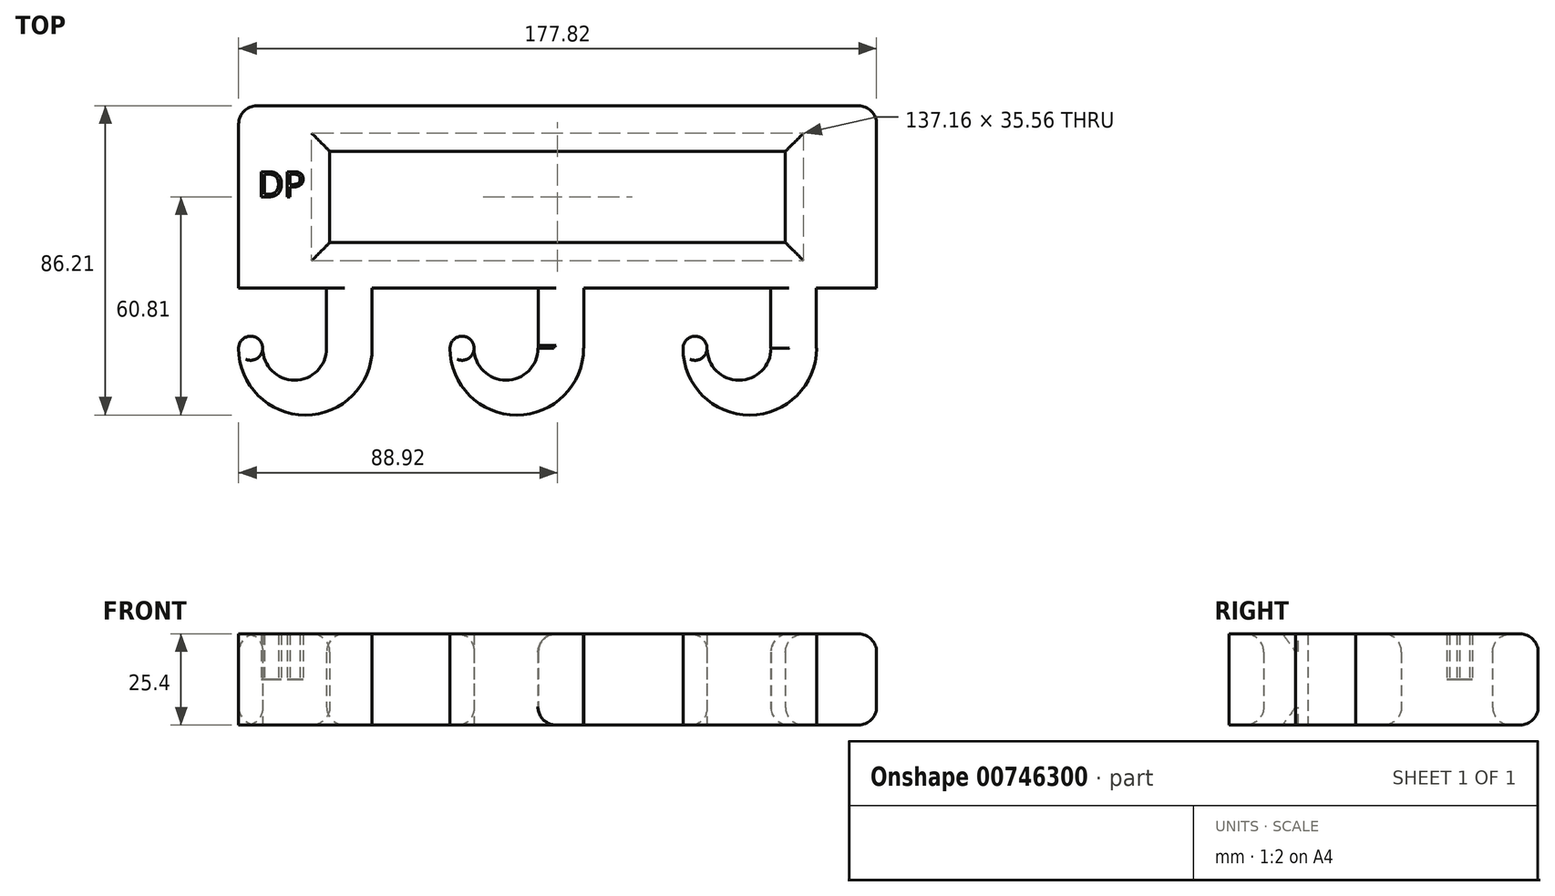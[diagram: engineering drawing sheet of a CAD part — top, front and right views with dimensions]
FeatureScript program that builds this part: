
annotation { "Feature Type Name" : "Feature", "Feature Type Description" : "" }
export const myFeature = defineFeature(function(context is Context, id is Id, definition is map)
    precondition{}
    {
        {
            var Q0;
            Q0=qCreatedBy(makeId("Top.planeOp"),FACE);
            var sketch = newSketch(context, id + "F0", { "sketchPlane" : qUnion([Q0])});
            skLineSegment(sketch, "E0.bottom", {"start": v(-88.9, 25.4) * mm, "end": v(88.9, 25.4) * mm});
            skLineSegment(sketch, "E0.top", {"start": v(-88.9, -25.4) * mm, "end": v(88.9, -25.4) * mm});
            skLineSegment(sketch, "E0.left", {"start": v(-88.9, 25.4) * mm, "end": v(-88.9, -25.4) * mm});
            skLineSegment(sketch, "E0.right", {"start": v(88.9, 25.4) * mm, "end": v(88.9, -25.4) * mm});
            skPoint(sketch, "E0.middle", {"position": v(0, 0) * mm});
            skLineSegment(sketch, "E1.bottom", {"start": v(-63.5, 12.7) * mm, "end": v(63.5, 12.7) * mm});
            skLineSegment(sketch, "E1.top", {"start": v(-63.5, -12.7) * mm, "end": v(63.5, -12.7) * mm});
            skLineSegment(sketch, "E1.left", {"start": v(-63.5, 12.7) * mm, "end": v(-63.5, -12.7) * mm});
            skLineSegment(sketch, "E1.right", {"start": v(63.5, 12.7) * mm, "end": v(63.5, -12.7) * mm});
            skLineSegment(sketch, "E2", {"start": v(-64.4, -25.4) * mm, "end": v(-64.4, -42.2) * mm});
            skLineSegment(sketch, "E3", {"start": v(-51.7, -42.2) * mm, "end": v(-51.7, -25.4) * mm});
            skLineSegment(sketch, "E4", {"start": v(-5.35, -25.4) * mm, "end": v(-5.35, -42.2) * mm});
            skLineSegment(sketch, "E5", {"start": v(-5.35, -42.2) * mm, "end": v(7.35, -42.2) * mm});
            skLineSegment(sketch, "E6", {"start": v(7.35, -42.2) * mm, "end": v(7.35, -25.4) * mm});
            skLineSegment(sketch, "E7", {"start": v(59.41, -25.4) * mm, "end": v(59.41, -42.2) * mm});
            skLineSegment(sketch, "E8", {"start": v(59.41, -42.2) * mm, "end": v(72.11, -42.2) * mm});
            skLineSegment(sketch, "E9", {"start": v(72.11, -42.2) * mm, "end": v(72.11, -25.4) * mm});
            skArc(sketch, "E10", {"start": v(-88.92, -42.2) * mm, "mid": v(-70.3, -60.81) * mm, "end": v(-51.7, -42.2) * mm});
            skArc(sketch, "E11", {"start": v(-82.2, -42.2) * mm, "mid": v(-73.3, -51.1) * mm, "end": v(-64.4, -42.2) * mm});
            skArc(sketch, "E12", {"start": v(-82.2, -42.2) * mm, "mid": v(-85.56, -38.83) * mm, "end": v(-88.92, -42.2) * mm});
            skArc(sketch, "E13", {"start": v(-30, -42.2) * mm, "mid": v(-11.4, -60.81) * mm, "end": v(7.22, -42.2) * mm});
            skArc(sketch, "E14", {"start": v(-23.3, -42.2) * mm, "mid": v(-14.39, -51.1) * mm, "end": v(-5.48, -42.2) * mm});
            skArc(sketch, "E15", {"start": v(-23.3, -42.2) * mm, "mid": v(-26.65, -38.83) * mm, "end": v(-30, -42.2) * mm});
            skLineSegment(sketch, "E16", {"start": v(-5.48, -42.2) * mm, "end": v(7.35, -42.2) * mm});
            skArc(sketch, "E17", {"start": v(34.94, -42.2) * mm, "mid": v(53.55, -60.81) * mm, "end": v(72.16, -42.2) * mm});
            skArc(sketch, "E18", {"start": v(41.65, -42.2) * mm, "mid": v(50.56, -51.1) * mm, "end": v(59.46, -42.2) * mm});
            skArc(sketch, "E19", {"start": v(41.65, -42.2) * mm, "mid": v(38.3, -38.83) * mm, "end": v(34.94, -42.2) * mm});
            skLineSegment(sketch, "E20", {"start": v(59.41, -42.2) * mm, "end": v(72.16, -42.2) * mm});
            skSolve(sketch);
        }
        {
            var Q0;
            Q0 = qSketchRegion(id + "F0", true);
            extrude(context, id + "F1", {"entities" : qUnion([Q0]), "endBound" : BoundingType.SYMMETRIC, "depth" : 25.4 * mm, "offsetDistance" : 25.4 * mm});
        }
        {
            var Q0;
            Q0=makeQuery(id+"F1.opExtrude","CAP_EDGE",EDGE,{"disambiguationData":[OSD([sQuery(id+"F0.wireOp",EDGE,"E1.left")])],"isStart":false});
            var Q1;
            Q1=makeQuery(id+"F1.opExtrude","CAP_EDGE",EDGE,{"disambiguationData":[OSD([sQuery(id+"F0.wireOp",EDGE,"E1.bottom")])],"isStart":false});
            var Q2;
            Q2=makeQuery(id+"F1.opExtrude","CAP_EDGE",EDGE,{"disambiguationData":[OSD([sQuery(id+"F0.wireOp",EDGE,"E1.right")])],"isStart":false});
            var Q3;
            Q3=makeQuery(id+"F1.opExtrude","CAP_EDGE",EDGE,{"disambiguationData":[OSD([sQuery(id+"F0.wireOp",EDGE,"E1.top")])],"isStart":false});
            var Q4;
            Q4=makeQuery(id+"F1.opExtrude","CAP_EDGE",EDGE,{"disambiguationData":[OSD([sQuery(id+"F0.wireOp",EDGE,"E1.top")])],"isStart":true});
            var Q5;
            Q5=makeQuery(id+"F1.opExtrude","CAP_EDGE",EDGE,{"disambiguationData":[OSD([sQuery(id+"F0.wireOp",EDGE,"E1.right")])],"isStart":true});
            var Q6;
            Q6=makeQuery(id+"F1.opExtrude","CAP_EDGE",EDGE,{"disambiguationData":[OSD([sQuery(id+"F0.wireOp",EDGE,"E1.bottom")])],"isStart":true});
            var Q7;
            Q7=makeQuery(id+"F1.opExtrude","CAP_EDGE",EDGE,{"disambiguationData":[OSD([sQuery(id+"F0.wireOp",EDGE,"E1.left")])],"isStart":true});
            var Q8;
            Q8=makeQuery(id+"F1.opExtrude","CAP_EDGE",EDGE,{"disambiguationData":[OSD([sQuery(id+"F0.wireOp",EDGE,"E0.bottom")])],"isStart":false});
            var Q9;
            Q9=makeQuery(id+"F1.opExtrude","CAP_EDGE",EDGE,{"disambiguationData":[OSD([sQuery(id+"F0.wireOp",EDGE,"E0.bottom")])],"isStart":true});
            var Q10;
            Q10=makeQuery(id+"F1.opExtrude","SWEPT_EDGE",EDGE,{"disambiguationData":[OSD([sQuery(id+"F0.wireOp",EDGE,"E0.bottom"),sQuery(id+"F0.wireOp",EDGE,"E0.left")])]});
            var Q11;
            Q11=makeQuery(id+"F1.opExtrude","SWEPT_EDGE",EDGE,{"disambiguationData":[OSD([sQuery(id+"F0.wireOp",EDGE,"E0.bottom"),sQuery(id+"F0.wireOp",EDGE,"E0.right")])]});
            var Q12;
            Q12=makeQuery(id+"F1.opExtrude","CAP_EDGE",EDGE,{"disambiguationData":[OSD([sQuery(id+"F0.wireOp",EDGE,"E0.left")])],"isStart":false});
            var Q13;
            Q13=makeQuery(id+"F1.opExtrude","CAP_EDGE",EDGE,{"disambiguationData":[OSD([sQuery(id+"F0.wireOp",EDGE,"E0.left")])],"isStart":true});
            var Q14;
            Q14=makeQuery(id+"F1.opExtrude","CAP_EDGE",EDGE,{"disambiguationData":[OSD([sQuery(id+"F0.wireOp",EDGE,"E0.right")])],"isStart":false});
            var Q15;
            Q15=makeQuery(id+"F1.opExtrude","CAP_EDGE",EDGE,{"disambiguationData":[OSD([sQuery(id+"F0.wireOp",EDGE,"E0.right")])],"isStart":true});
            fillet(context, id + "F2", {"entities" : qUnion([Q0, Q1, Q2, Q3, Q4, Q5, Q6, Q7, Q8, Q9, Q10, Q11, Q12, Q13, Q14, Q15]), "radius" : 5.08 * mm, "tangentPropagation" : true, "allowEdgeOverflow" : false});
        }
        {
            var Q0;
            Q0=makeQuery(id+"F1.opExtrude","CAP_EDGE",EDGE,{"disambiguationData":[OSD([sQuery(id+"F0.wireOp",EDGE,"E11")])],"isStart":false});
            var Q1;
            Q1=makeQuery(id+"F1.opExtrude","CAP_EDGE",EDGE,{"disambiguationData":[OSD([sQuery(id+"F0.wireOp",EDGE,"E18")])],"isStart":false});
            var Q2;
            Q2=makeQuery(id+"F1.opExtrude","CAP_EDGE",EDGE,{"disambiguationData":[OSD([sQuery(id+"F0.wireOp",EDGE,"E11")])],"isStart":true});
            var Q3;
            Q3=makeQuery(id+"F1.opExtrude","CAP_EDGE",EDGE,{"disambiguationData":[OSD([sQuery(id+"F0.wireOp",EDGE,"E18")])],"isStart":true});
            fillet(context, id + "F3", {"entities" : qUnion([Q0, Q1, Q2, Q3]), "radius" : 5.08 * mm, "tangentPropagation" : true, "allowEdgeOverflow" : false});
        }
        {
            var Q0;
            Q0=makeQuery(id+"F1.opExtrude","CAP_EDGE",EDGE,{"disambiguationData":[OSD([sQuery(id+"F0.wireOp",EDGE,"E7")])],"isStart":false});
            var Q1;
            Q1=makeQuery(id+"F1.opExtrude","CAP_EDGE",EDGE,{"disambiguationData":[OSD([sQuery(id+"F0.wireOp",EDGE,"E7")])],"isStart":true});
            fillet(context, id + "F4", {"entities" : qUnion([Q0, Q1]), "radius" : 5.08 * mm, "tangentPropagation" : true, "allowEdgeOverflow" : false});
        }
        {
            var Q0;
            Q0=makeQuery(id+"F1.opExtrude","CAP_EDGE",EDGE,{"disambiguationData":[OSD([sQuery(id+"F0.wireOp",EDGE,"E14")])],"isStart":true});
            var Q1;
            Q1=makeQuery(id+"F1.opExtrude","CAP_EDGE",EDGE,{"disambiguationData":[OSD([sQuery(id+"F0.wireOp",EDGE,"E14")])],"isStart":false});
            fillet(context, id + "F5", {"entities" : qUnion([Q0, Q1]), "radius" : 5.08 * mm, "tangentPropagation" : true, "allowEdgeOverflow" : false});
        }
        {
            var Q0;
            Q0=makeQuery(id+"F5.opFillet","BLEND_EDGE",EDGE,{"blendedFrom":[makeQuery(id+"F1.opExtrude","CAP_EDGE",EDGE,{"disambiguationData":[OSD([sQuery(id+"F0.wireOp",EDGE,"E14")])],"isStart":true}),makeQuery(id+"F1.opExtrude","SWEPT_FACE",FACE,{"disambiguationData":[OSD([sQuery(id+"F0.wireOp",EDGE,"E4")])]})],"blendedInto":[makeQuery(id+"F1.opExtrude","SWEPT_FACE",FACE,{"disambiguationData":[OSD([sQuery(id+"F0.wireOp",EDGE,"E4")])]})]});
            var Q1;
            Q1=makeQuery(id+"F5.opFillet","BLEND_EDGE",EDGE,{"blendedFrom":[makeQuery(id+"F1.opExtrude","CAP_EDGE",EDGE,{"disambiguationData":[OSD([sQuery(id+"F0.wireOp",EDGE,"E14")])],"isStart":false}),makeQuery(id+"F1.opExtrude","SWEPT_FACE",FACE,{"disambiguationData":[OSD([sQuery(id+"F0.wireOp",EDGE,"E4")])]})],"blendedInto":[makeQuery(id+"F1.opExtrude","SWEPT_FACE",FACE,{"disambiguationData":[OSD([sQuery(id+"F0.wireOp",EDGE,"E4")])]})]});
            var Q2;
            Q2=makeQuery(id+"F1.opExtrude","CAP_EDGE",EDGE,{"disambiguationData":[OSD([sQuery(id+"F0.wireOp",EDGE,"E4")])],"isStart":true});
            var Q3;
            Q3=makeQuery(id+"F1.opExtrude","CAP_EDGE",EDGE,{"disambiguationData":[OSD([sQuery(id+"F0.wireOp",EDGE,"E4")])],"isStart":false});
            fillet(context, id + "F6", {"entities" : qUnion([Q0, Q1, Q2, Q3]), "radius" : 4.93 * mm, "tangentPropagation" : true, "allowEdgeOverflow" : false});
        }
        {
            var Q0;
            Q0=qCreatedBy(makeId("Top.planeOp"),FACE);
            var sketch = newSketch(context, id + "F7", { "sketchPlane" : qUnion([Q0])});
            skText(sketch, "E21", { "text": "DP", "fontName": "OpenSans-Regular.ttf"});
            const initialGuessF7  = {"E21": [-0.08355, 0, 1, 0, 0.0071]};
            skSetInitialGuess(sketch, initialGuessF7);
            skSolve(sketch);
        }
        {
            var Q0;
            Q0 = qSketchRegion(id + "F7", true);
            extrude(context, id + "F8", {"entities" : qUnion([Q0]), "operationType" : NewBodyOperationType.REMOVE, "depth" : 25.4 * mm, "offsetDistance" : 25.4 * mm});
        }
    });
